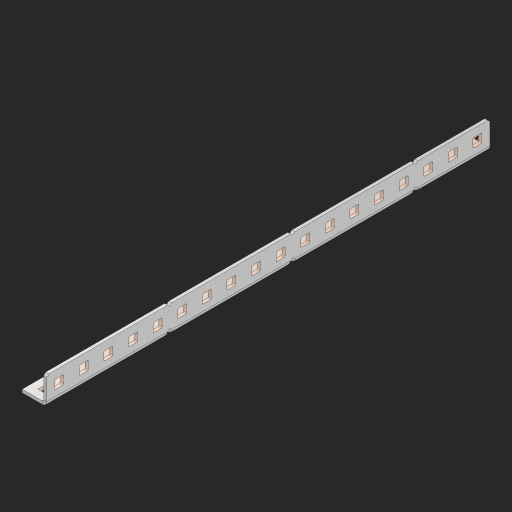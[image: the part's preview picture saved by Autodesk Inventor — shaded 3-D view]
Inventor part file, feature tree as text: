
AUTODESK INVENTOR PART (.ipt)
format: ipt  version: 2023 (Build 270158000, 158)  size: 724,992 bytes
history: native  units: in
note: dims shown in document units (in); Inventor stores cm internally (conversion verified against a paired STEP export)
features: other x41, extrude x35, sheet_metal_op x10, sketch x8, mirror x1, pattern_linear x1, chamfer x1
ambient origin geometry x8: Origin, YZ Plane, XZ Plane, XY Plane, X Axis, Y Axis, Z Axis, Center Point
bodies: Solid1 (feature_tree), Body (feature_tree)
feature tree (97):
  other  "Flange Pattern Plane"
  sheet_metal_op  "Flange Pattern"
  sheet_metal_op  "Body Pattern"
  other  "Arc Length"
  mirror  "Notch Mirror"
  pattern_linear  "Notch Pattern"  Spacing1=0.25in  [1 undecoded]
  chamfer  "End Chamfer"
  extrude  "Half Cut"  Depth=0.0625in
  sketch  "Sketch1"  dims[d0=1.5in]
  other  "Plate1"
  sketch  "Sketch2"  dims[d1=9.0in]
  other  "Plate2"
  sheet_metal_op  "Bend1"
  sheet_metal_op  "Corner1"
  sketch  "Sketch3"  dims[d2=0.0625in]
  other  "Flange Pattern Sketch"
  sketch  "Sketch7"  dims[d3=0.0625in]
  other  "Srf1"
  other  "Srf2"
  sketch  "Sketch8"  dims[d4=0.0312in]
  sketch  "Sketch9"  dims[d5=0.125in]
  other  "Srf91"
  sheet_metal_op  "Body Pattern Sketch"
  other  "Srf92"
  sketch  "Sketch13"  dims[d6=0.0625in]
  sketch  "Sketch14"  dims[d7=0.5in d8=90.0deg d9=0.0312in d10=0.25in d11=0.0625in d12=0.0625in d16=0.182in d17=0.02in d18=0.0625in d19=0.0in d20=0.25in d21=0.25in d46=0.172in d47=1.0in d48=0.0in d49=0.182in d50=0.02in d51=0.25in d52=0.25in d53=0.0625in d54=0.0in d55=0.172in d56=1.0in d57=0.0in d60=7.0866in d62=0.5in d63=0.3937in d65=0.5in d85=0.1473in d86=0.1782in d88=0.04in d89=0.0625in d90=0.0in d91=0.04in d92=0.0491in d95=2.5in d96=0.04in d97=0.25in d98=45.0deg d101=0.0in d102=2.497in d131=0.5in d132=7.0866in d134=0.5in d139=0.5in]
  other  "Srf856"
  other  "Srf1310"
  other  "Srf1311"
  other  "Srf1312"
  other  "Srf1376"
  other  "Srf1377"
  other  "Srf1728"
  other  "Srf1755"
  other  "Srf1878"
  other  "Srf1879"
  other  "Srf1880"
  other  "Srf1881"
  other  "Srf1882"
  other  "Srf1883"
  other  "Srf1884"
  other  "Srf1885"
  other  "Srf1886"
  other  "Srf1887"
  other  "Srf1888"
  other  "Srf1889"
  other  "Srf1942"
  other  "Srf1943"
  other  "Srf1944"
  other  "Srf1945"
  other  "Srf1946"
  other  "Srf1947"
  other  "Srf1948"
  other  "Srf1949"
  other  "Srf1950"
  other  "Srf1951"
  other  "Srf1952"
  other  "Srf1953"
  sheet_metal_op  "Flange Stamp"
  sheet_metal_op  "Flange Circle"
  sheet_metal_op  "Body Stamp"
  sheet_metal_op  "Body Circle"
  sheet_metal_op  "Notch"
  extrude  "ExtrusionSrf2"  Depth=0.0625in
  extrude  "ExtrusionSrf92"  Depth=0.5in
  extrude  "ExtrusionSrf856"  Depth=0.02in
  extrude  "ExtrusionSrf1310"  Depth=0.0625in
  extrude  "ExtrusionSrf1311"  TaperAngle=0.0deg  [1 undecoded]
  extrude  "ExtrusionSrf1312"  Depth=0.5in
  extrude  "ExtrusionSrf1376"  Depth=0.5in
  extrude  "ExtrusionSrf1377"  Depth=0.5in
  extrude  "ExtrusionSrf1728"  Depth=0.5in TaperAngle=0.0deg
  extrude  "ExtrusionSrf1755"  Depth=0.5in
  extrude  "ExtrusionSrf1878"  Depth=0.02in
  extrude  "ExtrusionSrf1879"  Depth=0.5in
  extrude  "ExtrusionSrf1880"  Depth=0.5in
  extrude  "ExtrusionSrf1881"  Depth=0.0625in
  extrude  "ExtrusionSrf1882"  TaperAngle=0.0deg  [1 undecoded]
  extrude  "ExtrusionSrf1883"  Depth=0.5in
  extrude  "ExtrusionSrf1884"  Depth=0.5in TaperAngle=0.0deg
  extrude  "ExtrusionSrf1885"  Depth=0.5in
  extrude  "ExtrusionSrf1886"  Depth=0.5in
  extrude  "ExtrusionSrf1887"  Depth=0.5in
  extrude  "ExtrusionSrf1888"  Depth=0.5in
  extrude  "ExtrusionSrf1889"  Depth=0.5in
  extrude  "ExtrusionSrf1942"  Depth=0.0625in
  extrude  "ExtrusionSrf1943"  TaperAngle=0.0deg  [1 undecoded]
  extrude  "ExtrusionSrf1944"  Depth=0.5in
  extrude  "ExtrusionSrf1945"  Depth=0.5in
  extrude  "ExtrusionSrf1946"  Depth=0.5in
  extrude  "ExtrusionSrf1947"  Depth=0.5in TaperAngle=45.0deg
  extrude  "ExtrusionSrf1948"  TaperAngle=0.0deg  [1 undecoded]
  extrude  "ExtrusionSrf1949"  Depth=0.5in
  extrude  "ExtrusionSrf1950"  Depth=0.5in
  extrude  "ExtrusionSrf1951"  Depth=0.5in
  extrude  "ExtrusionSrf1952"  Depth=0.5in
  extrude  "ExtrusionSrf1953"  Depth=0.5in
note: 5 required parameter values undecoded (feature->parameter linkage not recoverable at this tier; creation-order binding heuristic only, values carry confidence <= 0.55)
